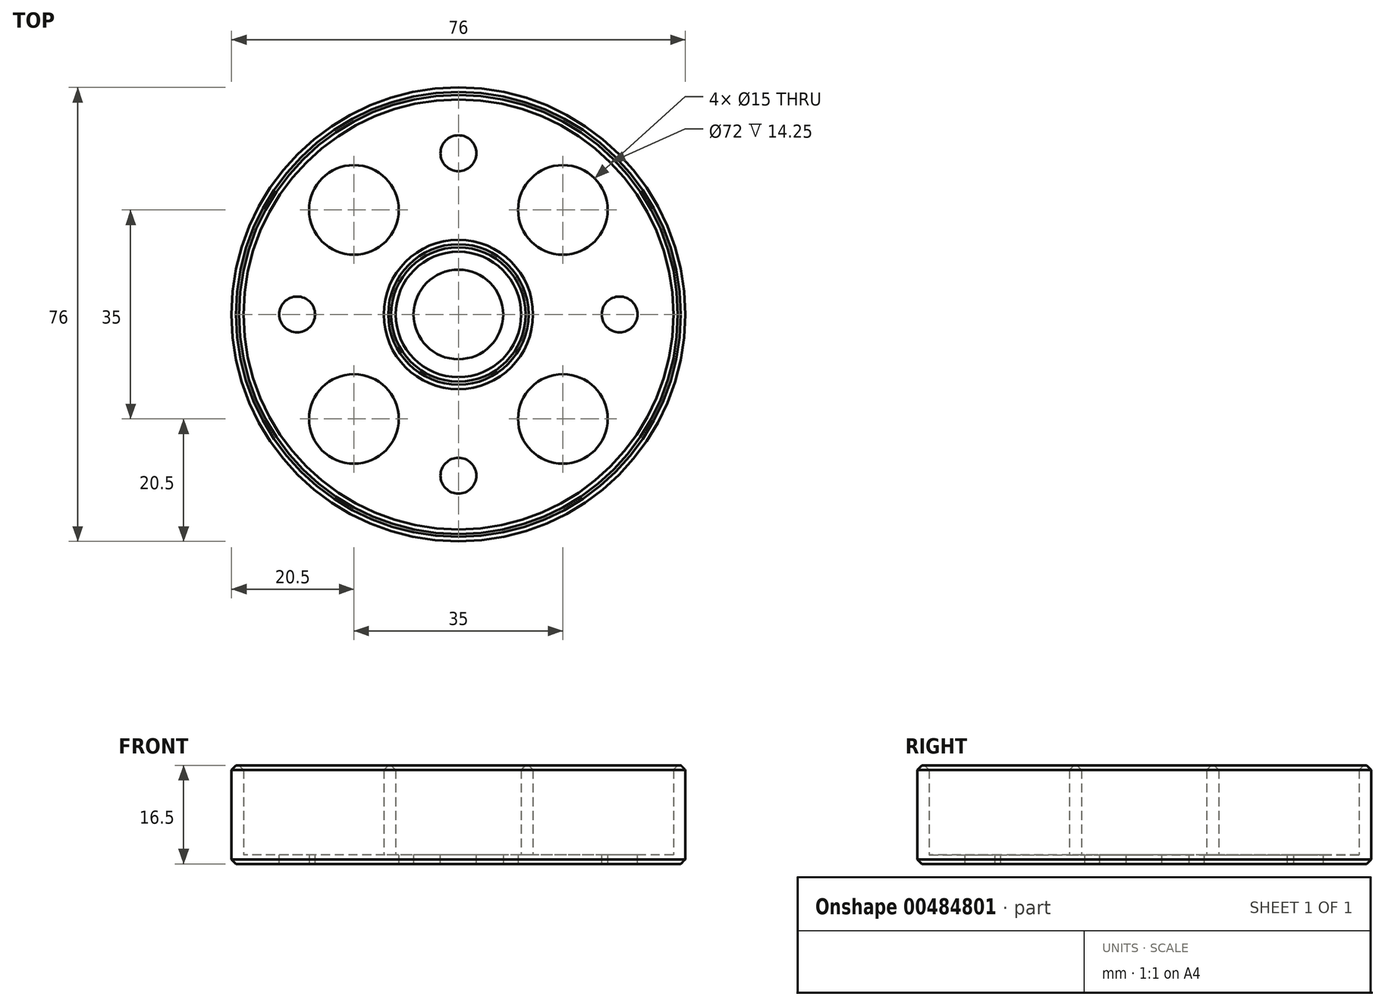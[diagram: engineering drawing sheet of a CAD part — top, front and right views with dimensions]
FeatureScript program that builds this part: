
annotation { "Feature Type Name" : "Feature", "Feature Type Description" : "" }
export const myFeature = defineFeature(function(context is Context, id is Id, definition is map)
    precondition{}
    {
        {
            var Q0;
            Q0=qCreatedBy(makeId("Top.planeOp"),FACE);
            var sketch = newSketch(context, id + "F0", { "sketchPlane" : qUnion([Q0])});
            skCircle(sketch, "E0", {"center": v(0, 0) * mm, "radius": 38 * mm});
            skCircle(sketch, "E1", {"center": v(-17.5, 17.5) * mm, "radius": 7.5 * mm});
            skLineSegment(sketch, "E2", {"start": v(0, 0) * mm, "end": v(17.5, 0) * mm, "construction": true});
            skLineSegment(sketch, "E3", {"start": v(17.5, 0) * mm, "end": v(17.5, 17.5) * mm, "construction": true});
            skLineSegment(sketch, "E4", {"start": v(17.5, 17.5) * mm, "end": v(-17.5, 17.5) * mm, "construction": true});
            skLineSegment(sketch, "E5", {"start": v(-17.5, 17.5) * mm, "end": v(-17.5, -17.5) * mm, "construction": true});
            skLineSegment(sketch, "E6", {"start": v(-17.5, -17.5) * mm, "end": v(17.5, -17.5) * mm, "construction": true});
            skLineSegment(sketch, "E7", {"start": v(17.5, -17.5) * mm, "end": v(17.5, 0) * mm, "construction": true});
            skCircle(sketch, "E8", {"center": v(17.5, -17.5) * mm, "radius": 7.5 * mm});
            skCircle(sketch, "E9", {"center": v(17.5, 17.5) * mm, "radius": 7.5 * mm});
            skCircle(sketch, "E10", {"center": v(-17.5, -17.5) * mm, "radius": 7.5 * mm});
            skCircle(sketch, "E11", {"center": v(0, 0) * mm, "radius": 7.5 * mm});
            skSolve(sketch);
        }
        {
            var Q0;
            Q0=makeQuery(id+"F0.imprint","IMPRINT",FACE,{"disambiguationData":[TD([[makeQuery(id+"F0.imprint","IMPRINT",EDGE,{"derivedFrom":sQuery(id+"F0.wireOp",EDGE,"E0")}),1.0]])]});
            extrude(context, id + "F1", {"entities" : qUnion([Q0]), "depth" : 1.5 * mm});
        }
        {
            var Q0;
            Q0=makeQuery(id+"F1.opExtrude","CAP_FACE",FACE,{"disambiguationData":[OSD([sQuery(id+"F0.wireOp",EDGE,"E0"),sQuery(id+"F0.wireOp",EDGE,"E1"),sQuery(id+"F0.wireOp",EDGE,"E8"),sQuery(id+"F0.wireOp",EDGE,"E9"),sQuery(id+"F0.wireOp",EDGE,"E10"),sQuery(id+"F0.wireOp",EDGE,"E11")])],"isStart":false});
            var sketch = newSketch(context, id + "F2", { "sketchPlane" : qUnion([Q0])});
            skCircle(sketch, "E12", {"center": v(0, 0) * mm, "radius": 38 * mm});
            skCircle(sketch, "E13.0", {"center": v(0, 0) * mm, "radius": 36 * mm});
            skCircle(sketch, "E14", {"center": v(0, 0) * mm, "radius": 10.5 * mm});
            skCircle(sketch, "E15.0", {"center": v(0, 0) * mm, "radius": 12.5 * mm});
            skSolve(sketch);
        }
        {
            var Q0;
            Q0=makeQuery(id+"F2.imprint","IMPRINT",FACE,{"disambiguationData":[TD([[makeQuery(id+"F2.imprint","IMPRINT",EDGE,{"derivedFrom":sQuery(id+"F2.wireOp",EDGE,"E14")}),-1.0]])]});
            var Q1;
            Q1=makeQuery(id+"F2.imprint","IMPRINT",FACE,{"disambiguationData":[TD([[makeQuery(id+"F2.imprint","IMPRINT",EDGE,{"derivedFrom":sQuery(id+"F2.wireOp",EDGE,"E12")}),1.0]])]});
            extrude(context, id + "F3", {"entities" : qUnion([Q0, Q1]), "operationType" : NewBodyOperationType.ADD, "depth" : 15 * mm});
        }
        {
            var Q0;
            Q0=makeQuery(id+"F1.opExtrude","CAP_EDGE",EDGE,{"disambiguationData":[OSD([sQuery(id+"F0.wireOp",EDGE,"E0")])],"isStart":true});
            var Q1;
            Q1=makeQuery(id+"F3.opExtrude","CAP_EDGE",EDGE,{"disambiguationData":[OSD([sQuery(id+"F2.wireOp",EDGE,"E12")])],"isStart":false});
            var Q2;
            Q2=makeQuery(id+"F3.opExtrude","CAP_EDGE",EDGE,{"disambiguationData":[OSD([sQuery(id+"F2.wireOp",EDGE,"E13.0")])],"isStart":false});
            var Q3;
            Q3=makeQuery(id+"F3.opExtrude","CAP_EDGE",EDGE,{"disambiguationData":[OSD([sQuery(id+"F2.wireOp",EDGE,"E15.0")])],"isStart":false});
            var Q4;
            Q4=makeQuery(id+"F3.opExtrude","CAP_EDGE",EDGE,{"disambiguationData":[OSD([sQuery(id+"F2.wireOp",EDGE,"E14")])],"isStart":false});
            chamfer(context, id + "F4", {"entities" : qUnion([Q0, Q1, Q2, Q3, Q4]), "width" : .75 * mm, "tangentPropagation" : true});
        }
        {
            var Q0;
            {var subQ0=sQuery(id+"F0.wireOp",EDGE,"E10");var subQ1=sQuery(id+"F0.wireOp",EDGE,"E9");var subQ2=sQuery(id+"F0.wireOp",EDGE,"E8");var subQ3=sQuery(id+"F0.wireOp",EDGE,"E1");Q0=makeQuery(id+"F3.boolean.opBoolean","SPLIT",FACE,{"disambiguationData":[TD([makeQuery(id+"F1.opExtrude","SWEPT_FACE",FACE,{"disambiguationData":[OSD([subQ3])]})])],"derivedFrom":makeQuery(id+"F1.opExtrude","CAP_FACE",FACE,{"disambiguationData":[OSD([sQuery(id+"F0.wireOp",EDGE,"E0"),subQ3,subQ2,subQ1,subQ0,sQuery(id+"F0.wireOp",EDGE,"E11")])],"isStart":false})});}
            var sketch = newSketch(context, id + "F5", { "sketchPlane" : qUnion([Q0])});
            skCircle(sketch, "E16", {"center": v(-27, 0) * mm, "radius": 3 * mm});
            skPoint(sketch, "E17.center", {"position": v(0, 0) * mm});
            skCircle(sketch, "E18.1.0", {"center": v(0, -27) * mm, "radius": 3 * mm});
            skCircle(sketch, "E18.2.0", {"center": v(27, 0) * mm, "radius": 3 * mm});
            skCircle(sketch, "E18.3.0", {"center": v(0, 27) * mm, "radius": 3 * mm});
            skSolve(sketch);
        }
        {
            var Q0;
            Q0 = qSketchRegion(id + "F5", true);
            extrude(context, id + "F6", {"entities" : qUnion([Q0]), "operationType" : NewBodyOperationType.REMOVE, "endBound" : BoundingType.THROUGH_ALL, "oppositeDirection" : true, "depth" : 25 * mm});
        }
    });
